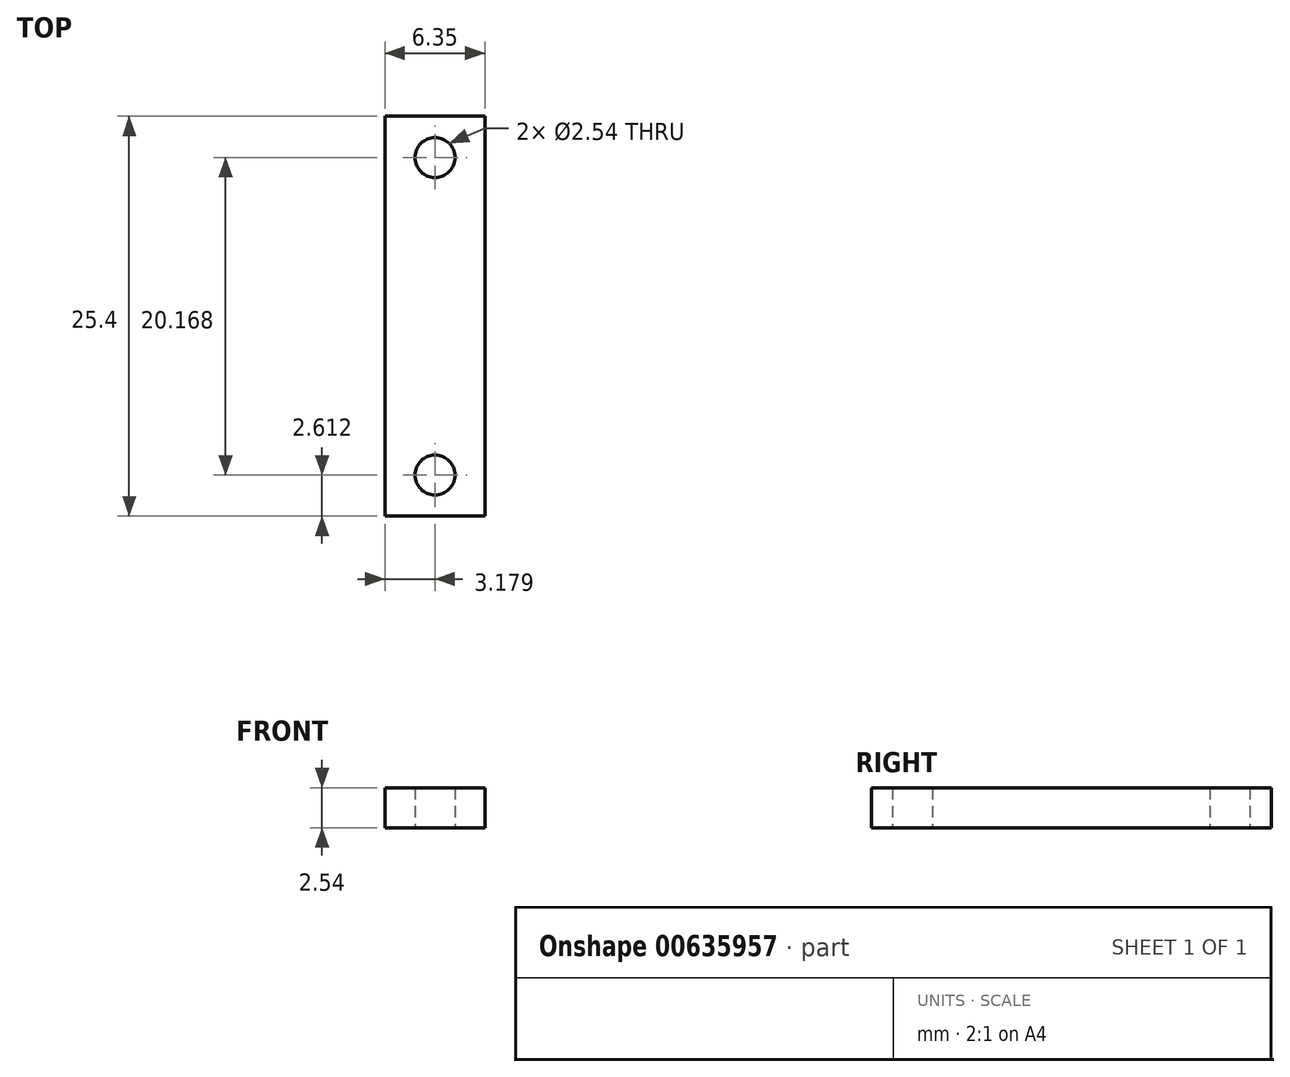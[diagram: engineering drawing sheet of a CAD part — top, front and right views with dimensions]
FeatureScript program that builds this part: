
annotation { "Feature Type Name" : "Feature", "Feature Type Description" : "" }
export const myFeature = defineFeature(function(context is Context, id is Id, definition is map)
    precondition{}
    {
        {
            var Q0;
            Q0=qCreatedBy(makeId("Top.planeOp"),FACE);
            var sketch = newSketch(context, id + "F0", { "sketchPlane" : qUnion([Q0])});
            skLineSegment(sketch, "E0.bottom", {"start": v(-44.82, 42.05) * mm, "end": v(-38.47, 42.05) * mm});
            skLineSegment(sketch, "E0.top", {"start": v(-44.82, 16.65) * mm, "end": v(-38.47, 16.65) * mm});
            skLineSegment(sketch, "E0.left", {"start": v(-44.82, 42.05) * mm, "end": v(-44.82, 16.65) * mm});
            skLineSegment(sketch, "E0.right", {"start": v(-38.47, 42.05) * mm, "end": v(-38.47, 16.65) * mm});
            skCircle(sketch, "E1", {"center": v(-41.64, 39.43) * mm, "radius": 1.27 * mm});
            skPoint(sketch, "E1.centerSnap0", {"position": v(-41.64, 42.05) * mm});
            skCircle(sketch, "E2", {"center": v(-41.64, 19.26) * mm, "radius": 1.27 * mm});
            skPoint(sketch, "E2.centerSnap0", {"position": v(-41.64, 16.65) * mm});
            skSolve(sketch);
        }
        {
            var Q0;
            Q0=makeQuery(id+"F0.imprint","IMPRINT",FACE,{"disambiguationData":[TD([[makeQuery(id+"F0.imprint","IMPRINT",EDGE,{"derivedFrom":sQuery(id+"F0.wireOp",EDGE,"E0.bottom")}),-1.0]])]});
            extrude(context, id + "F1", {"entities" : qUnion([Q0]), "depth" : 2.54 * mm, "offsetDistance" : 25.4 * mm});
        }
    });
